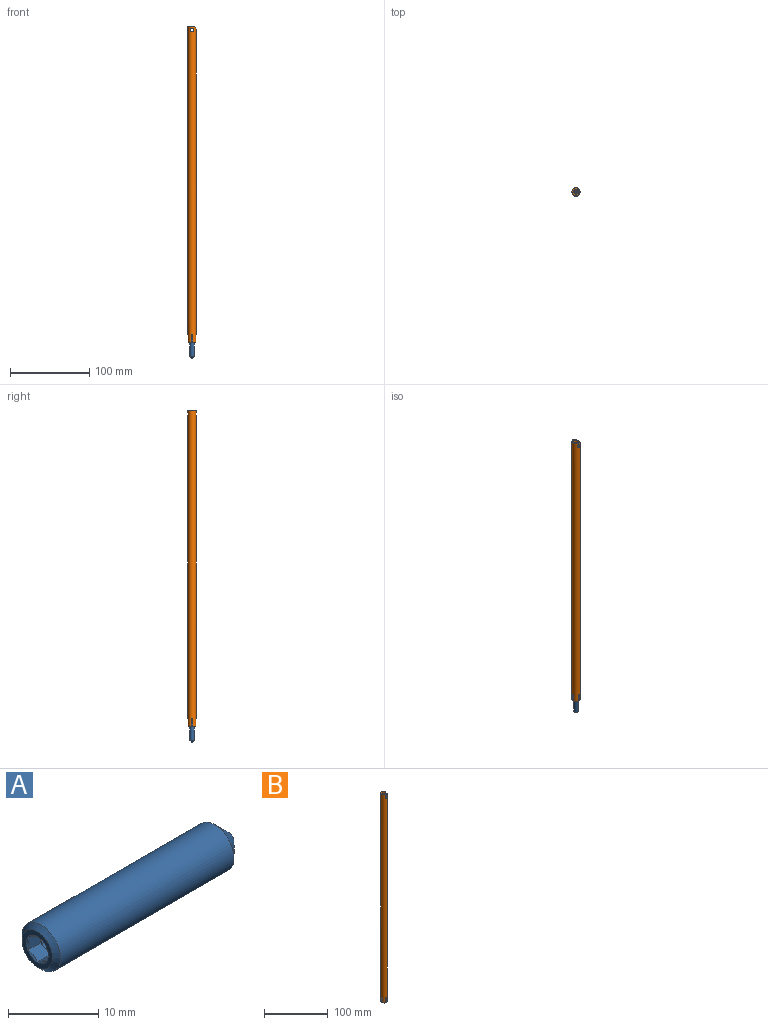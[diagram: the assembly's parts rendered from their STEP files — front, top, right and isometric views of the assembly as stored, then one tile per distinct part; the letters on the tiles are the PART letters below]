
ASSEMBLY  parts=2 mates=1
PART A: 25 faces, bbox 30x6x6 mm
  f0: cone r=1.73mm half-angle=45deg, axis (-1,0,0), area 0.4mm2, adj f10,f13
  f1: cone r=1.73mm half-angle=45deg, axis (-1,0,0), area 0.4mm2, adj f10,f14
  f2: cone r=1.73mm half-angle=45deg, axis (-1,0,0), area 0.4mm2, adj f10,f12
  f3: cone r=1.73mm half-angle=45deg, axis (-1,0,0), area 0.4mm2, adj f10,f15
  f4: cone r=1.73mm half-angle=45deg, axis (-1,0,0), area 0.4mm2, adj f10,f11
  f5: cone r=1.73mm half-angle=45deg, axis (-1,0,0), area 0.4mm2, adj f10,f16
  f6: plane 1.5x1.5mm, normal (1,0,0), area 1.8mm2, adj f7
  f7: cone r=0.75mm half-angle=45deg, axis (-1,0,0), area 37.5mm2, adj f6,f8
  f8: cylinder r=3mm len=27.14mm, axis (-1,0,0), area 511.5mm2, adj f7,f9
  f9: cone r=3mm half-angle=45deg, axis (1,0,0), area 14.7mm2, adj f8,f10
  f10: plane 4.77x4.77mm, normal (-1,0,0), area 8.5mm2, adj f0,f1,f2,f3,f4,f5,f9
  f11: plane 2x1.5mm, normal (0,-0.5,-0.87), area 3.2mm2, adj f4,f12,f16,f19,f20
  f12: plane 2x1.5mm, normal (0,0.5,-0.87), area 3.2mm2, adj f2,f11,f13,f18,f19
  f13: plane 2x1.74mm, normal (0,1,0), area 3.2mm2, adj f0,f12,f14,f17,f18
  f14: plane 2x1.5mm, normal (0,0.5,0.87), area 3.2mm2, adj f1,f13,f15,f17,f22
  f15: plane 2x1.5mm, normal (0,-0.5,0.87), area 3.2mm2, adj f3,f14,f16,f21,f22
  f16: plane 2x1.74mm, normal (0,-1,0), area 3.2mm2, adj f5,f11,f15,f20,f21
  f17: plane 1.3x0.75mm, normal (-1,0,0), area 0.1mm2, adj f13,f14,f24
  f18: plane 1.3x0.75mm, normal (-1,0,0), area 0.1mm2, adj f12,f13,f24
  f19: plane 1.5x0.43mm, normal (-1,0,0), area 0.1mm2, adj f11,f12,f24
  f20: plane 1.3x0.75mm, normal (-1,0,0), area 0.1mm2, adj f11,f16,f24
  f21: plane 1.3x0.75mm, normal (-1,0,0), area 0.1mm2, adj f15,f16,f24
  f22: plane 1.5x0.43mm, normal (-1,0,0), area 0.1mm2, adj f14,f15,f24
  f23: cone r=1.5mm half-angle=60deg, axis (-1,0,0), area 8.2mm2, adj f24
  f24: cylinder r=1.5mm len=3mm, axis (-1,0,0), area 9.4mm2, adj f17,f18,f19,f20,f21,f22,f23
PART B: 23 faces, bbox 10.2x10.2x400 mm
  f0: plane 4x4mm, normal (0,0,-1), area 8.8mm2, adj f1,f6,f12,f13
  f1: plane 10x2.07mm, normal (0,1,0), area 20.7mm2, adj f0,f3,f12,f13
  f2: plane 10x2.07mm, normal (0,-1,0), area 20.7mm2, adj f3,f12,f13,f14
  f3: plane 2.17x2mm, normal (0,0,-1), area 4mm2, adj f1,f2,f12,f13
  f4: plane 4x4mm, normal (0,0,-1), area 8.8mm2, adj f5,f10,f12,f13
  f5: plane 10x2.07mm, normal (-1,0,0), area 20.7mm2, adj f4,f7,f12,f13
  f6: plane 10x2.07mm, normal (1,0,0), area 20.7mm2, adj f0,f7,f12,f13
  f7: plane 2.17x2mm, normal (0,0,-1), area 4mm2, adj f5,f6,f12,f13
  f8: plane 4x4mm, normal (0,0,-1), area 8.8mm2, adj f9,f12,f13,f22
  f9: plane 10x2.07mm, normal (0,-1,0), area 20.7mm2, adj f8,f11,f12,f13
  f10: plane 10x2.07mm, normal (0,1,0), area 20.7mm2, adj f4,f11,f12,f13
  f11: plane 2.17x2mm, normal (0,0,-1), area 4mm2, adj f9,f10,f12,f13
  f12: cylinder r=3.1mm len=400mm, axis (0,0,-1), area 7675mm2, adj f0,f1,f2,f3,f4,f5,f6,f7
  f13: cylinder r=5.1mm len=400mm, axis (0,0,-1), area 12679.2mm2, adj f0,f1,f2,f3,f4,f5,f6,f7
  f14: plane 4x4mm, normal (0,0,-1), area 8.8mm2, adj f2,f12,f13,f21
  f15: plane 10.2x8.1mm, normal (0,0,1), area 39.5mm2, adj f12,f13,f17
  f16: cylinder r=5.1mm len=5.1mm, axis (0,-1,0), area 7mm2, adj f13,f17
  f17: plane 8.25x2.45mm, normal (0.87,0,0.5), area 19.3mm2, adj f12,f13,f15,f16
  f18: cylinder r=2.25mm len=4.5mm, axis (0,-1,0), area 31.1mm2, adj f12,f13
  f19: cylinder r=2.25mm len=4.5mm, axis (0,-1,0), area 31.2mm2, adj f12,f13
  f20: plane 2.17x2mm, normal (0,0,-1), area 4mm2, adj f12,f13,f21,f22
  f21: plane 10x2.07mm, normal (1,0,0), area 20.7mm2, adj f12,f13,f14,f20
  f22: plane 10x2.07mm, normal (-1,0,0), area 20.7mm2, adj f8,f12,f13,f20
PLACE A rot(axis=(-0.58,0.58,0.58),120deg) t=(0,0,10)mm
PLACE B at identity
MATE fastened A.f0 <-> B.f13  axis (0,0,1) through (0,0,10)mm
